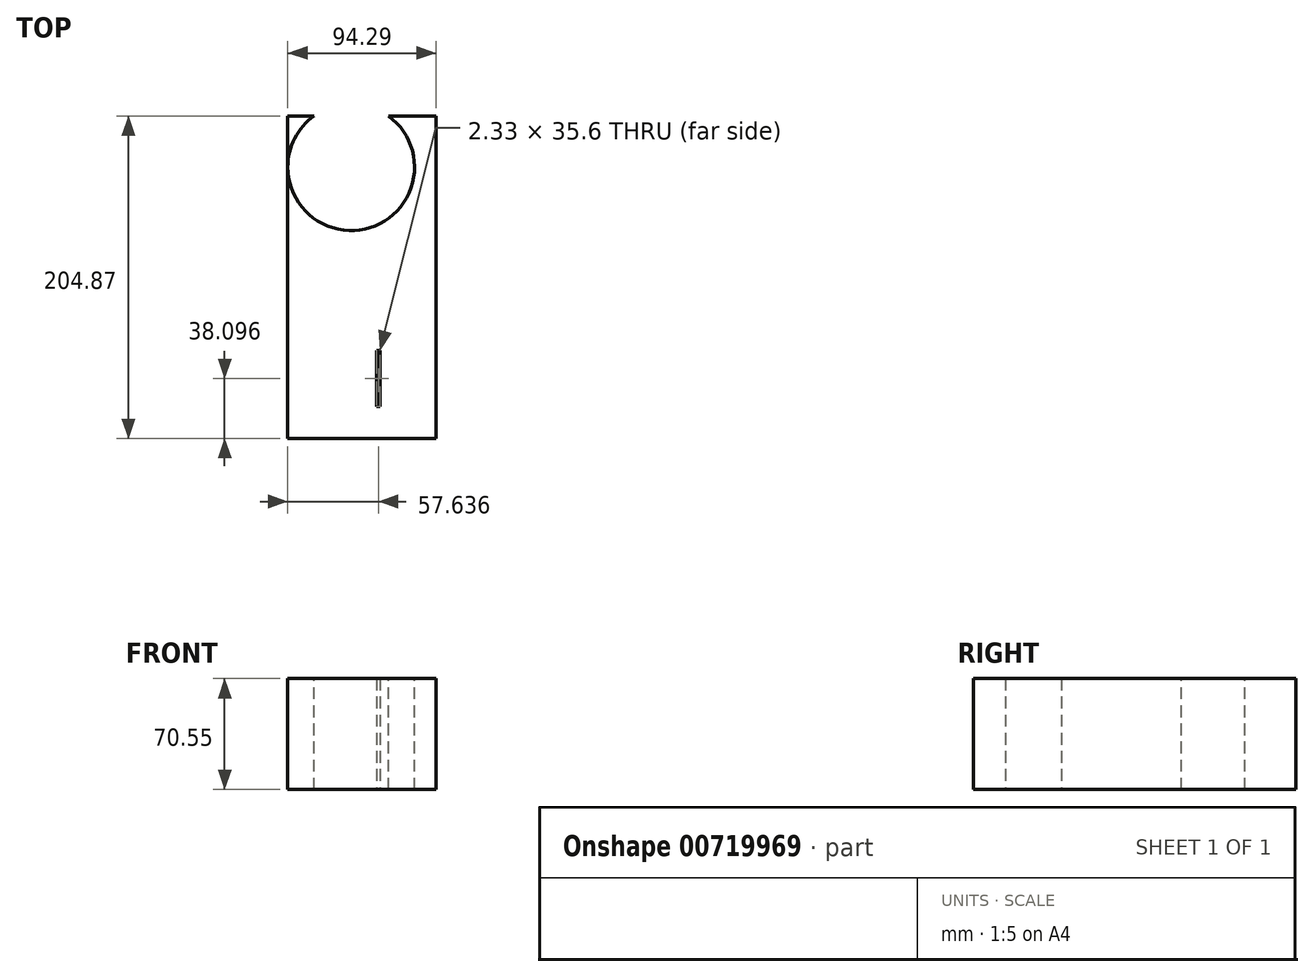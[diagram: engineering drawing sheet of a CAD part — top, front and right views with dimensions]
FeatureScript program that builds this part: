
annotation { "Feature Type Name" : "Feature", "Feature Type Description" : "" }
export const myFeature = defineFeature(function(context is Context, id is Id, definition is map)
    precondition{}
    {
        {
            var Q0;
            Q0=qCreatedBy(makeId("Top.planeOp"),FACE);
            var sketch = newSketch(context, id + "F0", { "sketchPlane" : qUnion([Q0])});
            skLineSegment(sketch, "E0.bottom", {"start": v(56.47, -231.17) * mm, "end": v(58.8, -231.17) * mm});
            skLineSegment(sketch, "E0.top", {"start": v(56.47, -266.78) * mm, "end": v(58.8, -266.78) * mm});
            skLineSegment(sketch, "E0.left", {"start": v(56.47, -231.17) * mm, "end": v(56.47, -266.78) * mm});
            skLineSegment(sketch, "E0.right", {"start": v(58.8, -231.17) * mm, "end": v(58.8, -266.78) * mm});
            skLineSegment(sketch, "E1.bottom", {"start": v(0, -82.2) * mm, "end": v(94.29, -82.2) * mm});
            skLineSegment(sketch, "E1.top", {"start": v(0, -287.07) * mm, "end": v(94.29, -287.07) * mm});
            skLineSegment(sketch, "E1.left", {"start": v(0, -82.2) * mm, "end": v(0, -287.07) * mm});
            skLineSegment(sketch, "E1.right", {"start": v(94.29, -82.2) * mm, "end": v(94.29, -287.07) * mm});
            skSolve(sketch);
        }
        {
            var Q0;
            Q0=makeQuery(id+"F0.imprint","IMPRINT",FACE,{"disambiguationData":[TD([[makeQuery(id+"F0.imprint","IMPRINT",EDGE,{"derivedFrom":sQuery(id+"F0.wireOp",EDGE,"E0.bottom")}),1.0]])]});
            extrude(context, id + "F1", {"entities" : qUnion([Q0]), "depth" : 70.55 * mm, "offsetDistance" : 25 * mm});
        }
        {
            var Q0;
            Q0=makeQuery(id+"F1.opExtrude","CAP_FACE",FACE,{"disambiguationData":[OSD([sQuery(id+"F0.wireOp",EDGE,"E0.bottom"),sQuery(id+"F0.wireOp",EDGE,"E0.top"),sQuery(id+"F0.wireOp",EDGE,"E0.left"),sQuery(id+"F0.wireOp",EDGE,"E0.right"),sQuery(id+"F0.wireOp",EDGE,"E1.bottom"),sQuery(id+"F0.wireOp",EDGE,"E1.top"),sQuery(id+"F0.wireOp",EDGE,"E1.left"),sQuery(id+"F0.wireOp",EDGE,"E1.right")])],"isStart":false});
            var sketch = newSketch(context, id + "F2", { "sketchPlane" : qUnion([Q0])});
            skCircle(sketch, "E2", {"center": v(40.25, -114.77) * mm, "radius": 40.25 * mm});
            skSolve(sketch);
        }
        {
            var Q0;
            {var subQ0=sQuery(id+"F2.wireOp",EDGE,"E2");var subQ1=makeQuery(id+"F1.opExtrude","CAP_EDGE",EDGE,{"disambiguationData":[OSD([sQuery(id+"F0.wireOp",EDGE,"E1.bottom")])],"isStart":false});var subQ2=makeQuery(id+"F2.imprint","INTERSECT",VERTEX,{"disambiguationData":[OD(0.0)],"derivedFrom":[subQ1,subQ0]});Q0=makeQuery(id+"F2.imprint","IMPRINT",FACE,{"disambiguationData":[TD([[makeQuery(id+"F2.imprint","IMPRINT",EDGE,{"disambiguationData":[TD([[subQ2,-1.0]])],"derivedFrom":subQ0}),1.0]])]});}
            extrude(context, id + "F3", {"entities" : qUnion([Q0]), "operationType" : NewBodyOperationType.REMOVE, "oppositeDirection" : true, "depth" : 90.98 * mm, "offsetDistance" : 25 * mm});
        }
    });
